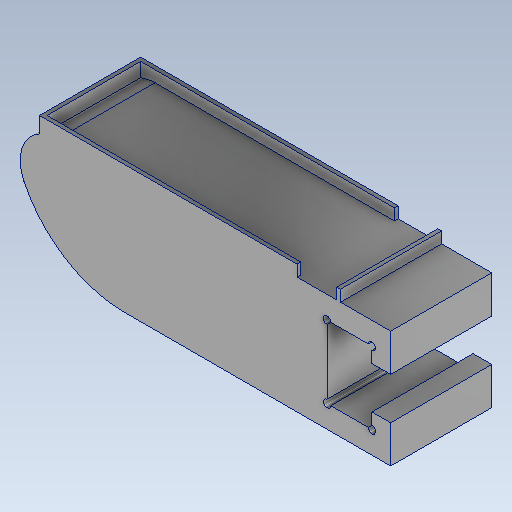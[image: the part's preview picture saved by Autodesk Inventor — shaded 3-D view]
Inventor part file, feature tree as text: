
AUTODESK INVENTOR PART (.ipt)
format: ipt  version: 2025.2 (Build 292293000, 293)  size: 445,952 bytes
history: native  units: mm
features: extrude x7, sketch x7, fillet x2
ambient origin geometry x8: Origin, YZ Plane, XZ Plane, XY Plane, X Axis, Y Axis, Z Axis, Center Point
bodies: Solid2 (feature_tree)
feature tree (16):
  extrude  "Extrusion2"  Depth=2.5mm
  fillet  "Fillet2"  Radius=2.5mm
  extrude  "Extrusion7"  Depth=15.6mm
  fillet  "Rundung3"  Radius=15.6mm
  extrude  "Extrusion12"  Depth=9.65mm
  extrude  "Extrusion13"  Depth=15.0mm
  extrude  "Extrusion14"  Depth=1.0mm
  extrude  "Extrusion15"  Depth=1.0mm
  extrude  "Extrusion16"  Depth=5.0mm
  sketch  "Sketch5"  dims[d41=6.0mm d48=42.0mm d50=2.5mm]
  sketch  "Sketch11"  dims[d56=13.5mm d57=0.0mm d63=44.7mm d67=15.6mm d71=0.0mm]
  sketch  "Skizze17"  dims[d87=5.6mm d88=9.65mm]
  sketch  "Skizze18"  dims[d97=15.6mm d98=15.0mm]
  sketch  "Skizze19"  dims[d99=1.0mm d100=1.0mm]
  sketch  "Skizze20"  dims[d101=1.0mm d102=1.0mm]
  sketch  "Skizze21"  dims[d103=0.0mm d104=0.0mm d105=5.0mm d122=1.5mm d123=1.0mm d124=39.5mm d125=38.5mm d127=1.0mm d128=5.5mm d129=3.0mm d130=0.0mm d131=1.5mm d132=0.0mm d133=3.0mm d134=0.0mm d135=3.0mm d136=0.0mm d137=0.0mm d139=0.5mm d140=0.5mm d143=3.0mm d144=0.0mm d150=0.0mm d152=5.3mm d159=0.5mm d160=0.5mm d161=0.0mm d162=0.0mm d163=1.92mm]
